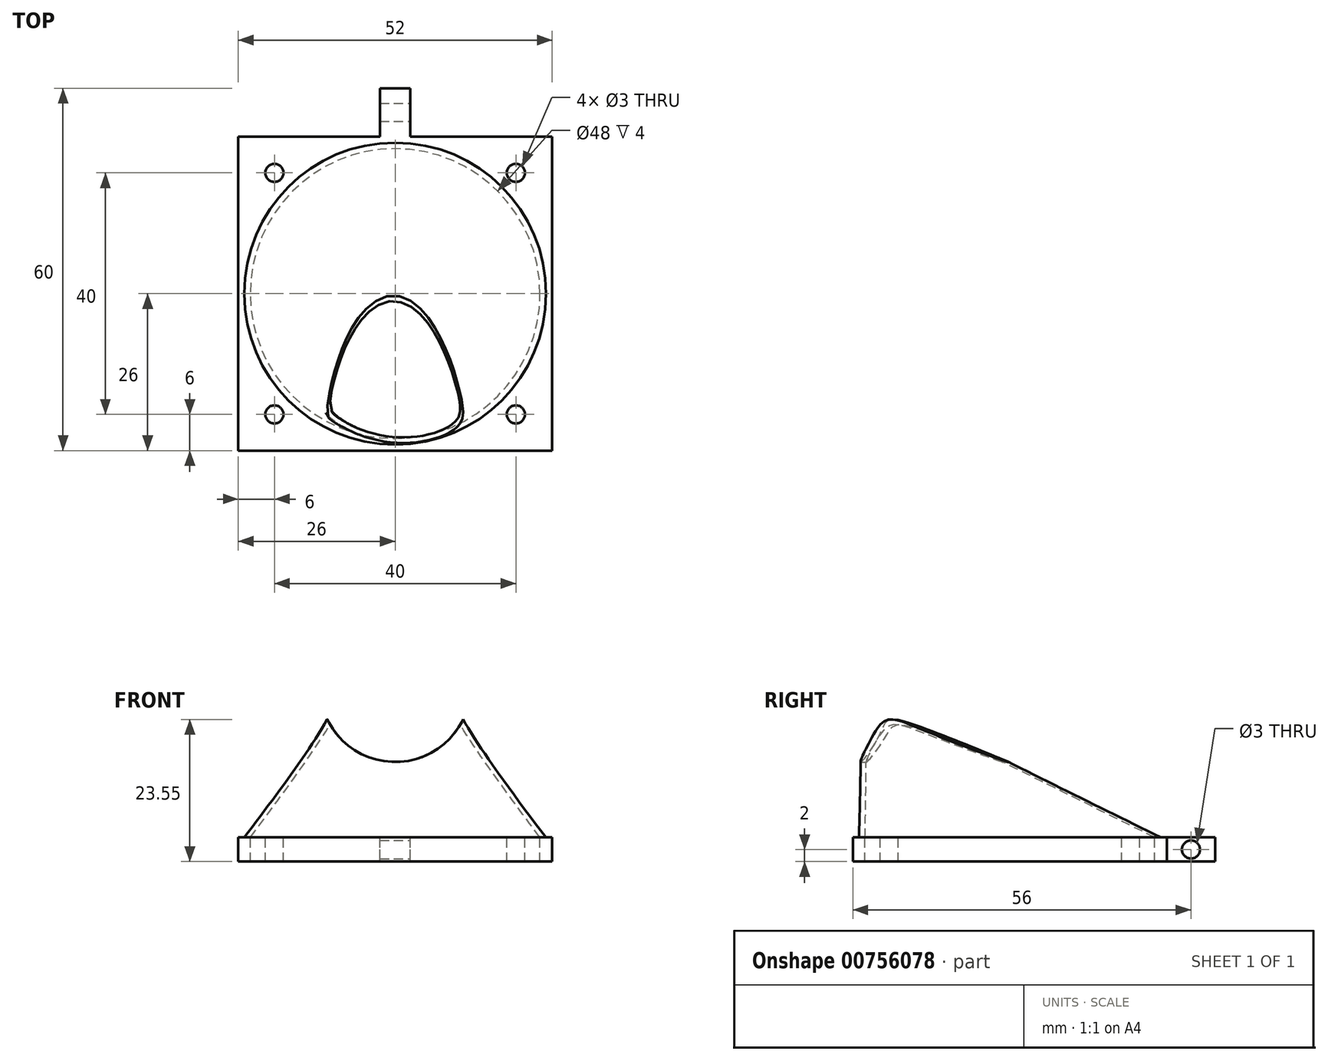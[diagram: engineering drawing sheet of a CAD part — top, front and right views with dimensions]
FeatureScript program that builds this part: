
annotation { "Feature Type Name" : "Feature", "Feature Type Description" : "" }
export const myFeature = defineFeature(function(context is Context, id is Id, definition is map)
    precondition{}
    {
        {
            var Q0;
            Q0=qCreatedBy(makeId("Top.planeOp"),FACE);
            var sketch = newSketch(context, id + "F0", { "sketchPlane" : qUnion([Q0])});
            skPoint(sketch, "E0.middle", {"position": v(0, 0) * mm});
            skCircle(sketch, "E1", {"center": v(0, 0) * mm, "radius": 24 * mm});
            skLineSegment(sketch, "E2.bottom", {"start": v(26, -26) * mm, "end": v(-26, -26) * mm});
            skLineSegment(sketch, "E2.top", {"start": v(26, 26) * mm, "end": v(-26, 26) * mm});
            skLineSegment(sketch, "E2.left", {"start": v(26, -26) * mm, "end": v(26, 26) * mm});
            skLineSegment(sketch, "E2.right", {"start": v(-26, -26) * mm, "end": v(-26, 26) * mm});
            skCircle(sketch, "E3", {"center": v(20, -20) * mm, "radius": 1.5 * mm});
            skCircle(sketch, "E4.MirrorC", {"center": v(-20, -20) * mm, "radius": 1.5 * mm});
            skCircle(sketch, "E5.MirrorC", {"center": v(20, 20) * mm, "radius": 1.5 * mm});
            skCircle(sketch, "E6.MirrorC", {"center": v(-20, 20) * mm, "radius": 1.5 * mm});
            skLineSegment(sketch, "E7.bottom", {"start": v(2.5, 26) * mm, "end": v(-2.5, 26) * mm});
            skLineSegment(sketch, "E7.top", {"start": v(2.5, 34) * mm, "end": v(-2.5, 34) * mm});
            skLineSegment(sketch, "E7.left", {"start": v(2.5, 26) * mm, "end": v(2.5, 34) * mm});
            skLineSegment(sketch, "E7.right", {"start": v(-2.5, 26) * mm, "end": v(-2.5, 34) * mm});
            skPoint(sketch, "E7.middle", {"position": v(0, 30) * mm});
            skLineSegment(sketch, "E8.0", {"start": v(2.5, 30) * mm, "end": v(-2.5, 30) * mm});
            skLineSegment(sketch, "E9.0", {"start": v(2.5, 31.5) * mm, "end": v(-2.5, 31.5) * mm});
            skLineSegment(sketch, "E10.0", {"start": v(2.5, 28.5) * mm, "end": v(-2.5, 28.5) * mm});
            skSolve(sketch);
        }
        {
            var Q0;
            Q0=qCreatedBy(makeId("Top.planeOp"),FACE);
            cPlane(context, id + "F1", {"entities" : qUnion([Q0]), "cplaneType" : CPlaneType.OFFSET, "offset" : 20 * mm, "width" : 150 * mm, "height" : 150 * mm});
        }
        {
            var Q0;
            Q0=qCreatedBy(id+"F1.planeOp",FACE);
            var sketch = newSketch(context, id + "F2", { "sketchPlane" : qUnion([Q0])});
            skEllipse(sketch, "E11", {"center": v(0, -20) * mm, "majorRadius": 10 * mm, "minorRadius": 4 * mm, "majorAxis": v(1, 0)});
            skSolve(sketch);
        }
        {
            var Q0;
            Q0=makeQuery(id+"F0.imprint","IMPRINT",FACE,{"disambiguationData":[TD([[makeQuery(id+"F0.imprint","IMPRINT",EDGE,{"derivedFrom":sQuery(id+"F0.wireOp",EDGE,"E1")}),1.0]])]});
            var Q1;
            Q1=makeQuery(id+"F2.imprint","IMPRINT",FACE,{"disambiguationData":[TD([[makeQuery(id+"F2.imprint","IMPRINT",EDGE,{"derivedFrom":sQuery(id+"F2.wireOp",EDGE,"E11")}),1.0]])]});
            loft(context, id + "F3", {"sheetProfilesArray" : [{ "sheetProfileEntities" : qUnion([Q0]) }, { "sheetProfileEntities" : qUnion([Q1]) }]});
        }
        {
            var Q0;
            Q0=qCreatedBy(makeId("Top.planeOp"),FACE);
            var sketch = newSketch(context, id + "F4", { "sketchPlane" : qUnion([Q0])});
            skCircle(sketch, "E12", {"center": v(0, 0) * mm, "radius": 25 * mm});
            skSolve(sketch);
        }
        {
            var Q0;
            Q0=qCreatedBy(id+"F1.planeOp",FACE);
            var sketch = newSketch(context, id + "F5", { "sketchPlane" : qUnion([Q0])});
            skEllipse(sketch, "E13", {"center": v(0, -20) * mm, "majorRadius": 11 * mm, "minorRadius": 5 * mm, "majorAxis": v(1, 0)});
            skSolve(sketch);
        }
        {
            var Q1;
            Q1=makeQuery(id+"F4.imprint","IMPRINT",FACE,{"disambiguationData":[TD([[makeQuery(id+"F4.imprint","IMPRINT",EDGE,{"derivedFrom":sQuery(id+"F4.wireOp",EDGE,"E12")}),1.0]])]});
            var Q2;
            Q2=makeQuery(id+"F5.imprint","IMPRINT",FACE,{"disambiguationData":[TD([[makeQuery(id+"F5.imprint","IMPRINT",EDGE,{"derivedFrom":sQuery(id+"F5.wireOp",EDGE,"E13")}),1.0]])]});
            loft(context, id + "F6", {"sheetProfilesArray" : [{ "sheetProfileEntities" : qUnion([Q1]) }, { "sheetProfileEntities" : qUnion([Q2]) }]});
        }
        {
            var Q0;
            Q0=makeQuery(id+"F3.opLoft","SWEPT_BODY",BODY,{"disambiguationData":[OSD([makeQuery(id+"F0.imprint","IMPRINT",FACE,{"disambiguationData":[TD([[makeQuery(id+"F0.imprint","IMPRINT",EDGE,{"derivedFrom":sQuery(id+"F0.wireOp",EDGE,"E1")}),1.0]])]}),makeQuery(id+"F2.imprint","IMPRINT",FACE,{"disambiguationData":[TD([[makeQuery(id+"F2.imprint","IMPRINT",EDGE,{"derivedFrom":sQuery(id+"F2.wireOp",EDGE,"E11")}),1.0]])]})])]});
            var Q1;
            Q1=makeQuery(id+"F6.opLoft","SWEPT_BODY",BODY,{"disambiguationData":[OSD([makeQuery(id+"F4.imprint","IMPRINT",FACE,{"disambiguationData":[TD([[makeQuery(id+"F4.imprint","IMPRINT",EDGE,{"derivedFrom":sQuery(id+"F4.wireOp",EDGE,"E12")}),1.0]])]}),makeQuery(id+"F5.imprint","IMPRINT",FACE,{"disambiguationData":[TD([[makeQuery(id+"F5.imprint","IMPRINT",EDGE,{"derivedFrom":sQuery(id+"F5.wireOp",EDGE,"E13")}),1.0]])]})])]});
            booleanBodies(context, id + "F7", {"operationType" : BooleanOperationType.SUBTRACTION, "tools" : qUnion([Q0]), "targets" : qUnion([Q1])});
        }
        {
            var Q0;
            Q0=makeQuery(id+"F0.imprint","IMPRINT",FACE,{"disambiguationData":[TD([[makeQuery(id+"F0.imprint","IMPRINT",EDGE,{"derivedFrom":sQuery(id+"F0.wireOp",EDGE,"E1")}),-1.0]])]});
            var Q1;
            {var subQ5=sQuery(id+"F0.wireOp",EDGE,"E10.0");Q1=makeQuery(id+"F0.imprint","IMPRINT",FACE,{"disambiguationData":[TD([[makeQuery(id+"F0.imprint","IMPRINT",EDGE,{"derivedFrom":subQ5}),1.0]])]});}
            var Q2;
            {var subQ0=sQuery(id+"F0.wireOp",EDGE,"E8.0");Q2=makeQuery(id+"F0.imprint","IMPRINT",FACE,{"disambiguationData":[TD([[makeQuery(id+"F0.imprint","IMPRINT",EDGE,{"derivedFrom":subQ0}),1.0]])]});}
            var Q3;
            {var subQ2=sQuery(id+"F0.wireOp",EDGE,"E8.0");Q3=makeQuery(id+"F0.imprint","IMPRINT",FACE,{"disambiguationData":[TD([[makeQuery(id+"F0.imprint","IMPRINT",EDGE,{"derivedFrom":subQ2}),-1.0]])]});}
            var Q4;
            {var subQ0=sQuery(id+"F0.wireOp",EDGE,"E7.top");Q4=makeQuery(id+"F0.imprint","IMPRINT",FACE,{"disambiguationData":[TD([[makeQuery(id+"F0.imprint","IMPRINT",EDGE,{"derivedFrom":subQ0}),1.0]])]});}
            extrude(context, id + "F8", {"entities" : qUnion([Q0, Q1, Q2, Q3, Q4]), "operationType" : NewBodyOperationType.ADD, "oppositeDirection" : true, "depth" : 4 * mm});
        }
        {
            var Q0;
            {var subQ0=sQuery(id+"F0.wireOp",EDGE,"E8.0");Q0=makeQuery(id+"F0.imprint","IMPRINT",FACE,{"disambiguationData":[TD([[makeQuery(id+"F0.imprint","IMPRINT",EDGE,{"derivedFrom":subQ0}),1.0]])]});}
            var Q1;
            Q1=sQuery(id+"F0.wireOp",EDGE,"E8.0");
            revolve(context, id + "F9", {"entities" : qUnion([Q0]), "axis" : qUnion([Q1]), "revolveType" : RevolveType.FULL});
        }
        {
            var Q0;
            Q0=makeQuery(id+"F9.opRevolve","SWEPT_BODY",BODY,{"disambiguationData":[OSD([sQuery(id+"F0.wireOp",EDGE,"E7.left"),sQuery(id+"F0.wireOp",EDGE,"E7.right"),sQuery(id+"F0.wireOp",EDGE,"E8.0"),sQuery(id+"F0.wireOp",EDGE,"E10.0")])]});
            transform(context, id + "F10", {"entities" : qUnion([Q0]), "transformType" : TransformType.TRANSLATION_3D, "dx" : 0 * mm, "dy" : 0 * mm, "dz" : -2 * mm, "makeCopy" : false});
        }
        {
            var Q0;
            Q0=makeQuery(id+"F9.opRevolve","SWEPT_BODY",BODY,{"disambiguationData":[OSD([sQuery(id+"F0.wireOp",EDGE,"E7.left"),sQuery(id+"F0.wireOp",EDGE,"E7.right"),sQuery(id+"F0.wireOp",EDGE,"E8.0"),sQuery(id+"F0.wireOp",EDGE,"E10.0")])]});
            var Q1;
            Q1=makeQuery(id+"F6.opLoft","SWEPT_BODY",BODY,{"disambiguationData":[OSD([makeQuery(id+"F4.imprint","IMPRINT",FACE,{"disambiguationData":[TD([[makeQuery(id+"F4.imprint","IMPRINT",EDGE,{"derivedFrom":sQuery(id+"F4.wireOp",EDGE,"E12")}),1.0]])]}),makeQuery(id+"F5.imprint","IMPRINT",FACE,{"disambiguationData":[TD([[makeQuery(id+"F5.imprint","IMPRINT",EDGE,{"derivedFrom":sQuery(id+"F5.wireOp",EDGE,"E13")}),1.0]])]})])]});
            booleanBodies(context, id + "F11", {"operationType" : BooleanOperationType.SUBTRACTION, "tools" : qUnion([Q0]), "targets" : qUnion([Q1])});
        }
        {
            var Q0;
            Q0=qCreatedBy(makeId("Front.planeOp"),FACE);
            var sketch = newSketch(context, id + "F12", { "sketchPlane" : qUnion([Q0])});
            skCircle(sketch, "E14", {"center": v(0, 25) * mm, "radius": 12.5 * mm});
            skSolve(sketch);
        }
        {
            var Q0;
            Q0=makeQuery(id+"F12.imprint","IMPRINT",FACE,{"disambiguationData":[TD([[makeQuery(id+"F12.imprint","IMPRINT",EDGE,{"derivedFrom":sQuery(id+"F12.wireOp",EDGE,"E14")}),1.0]])]});
            extrude(context, id + "F13", {"entities" : qUnion([Q0]), "operationType" : NewBodyOperationType.REMOVE, "depth" : 30 * mm});
        }
    });
